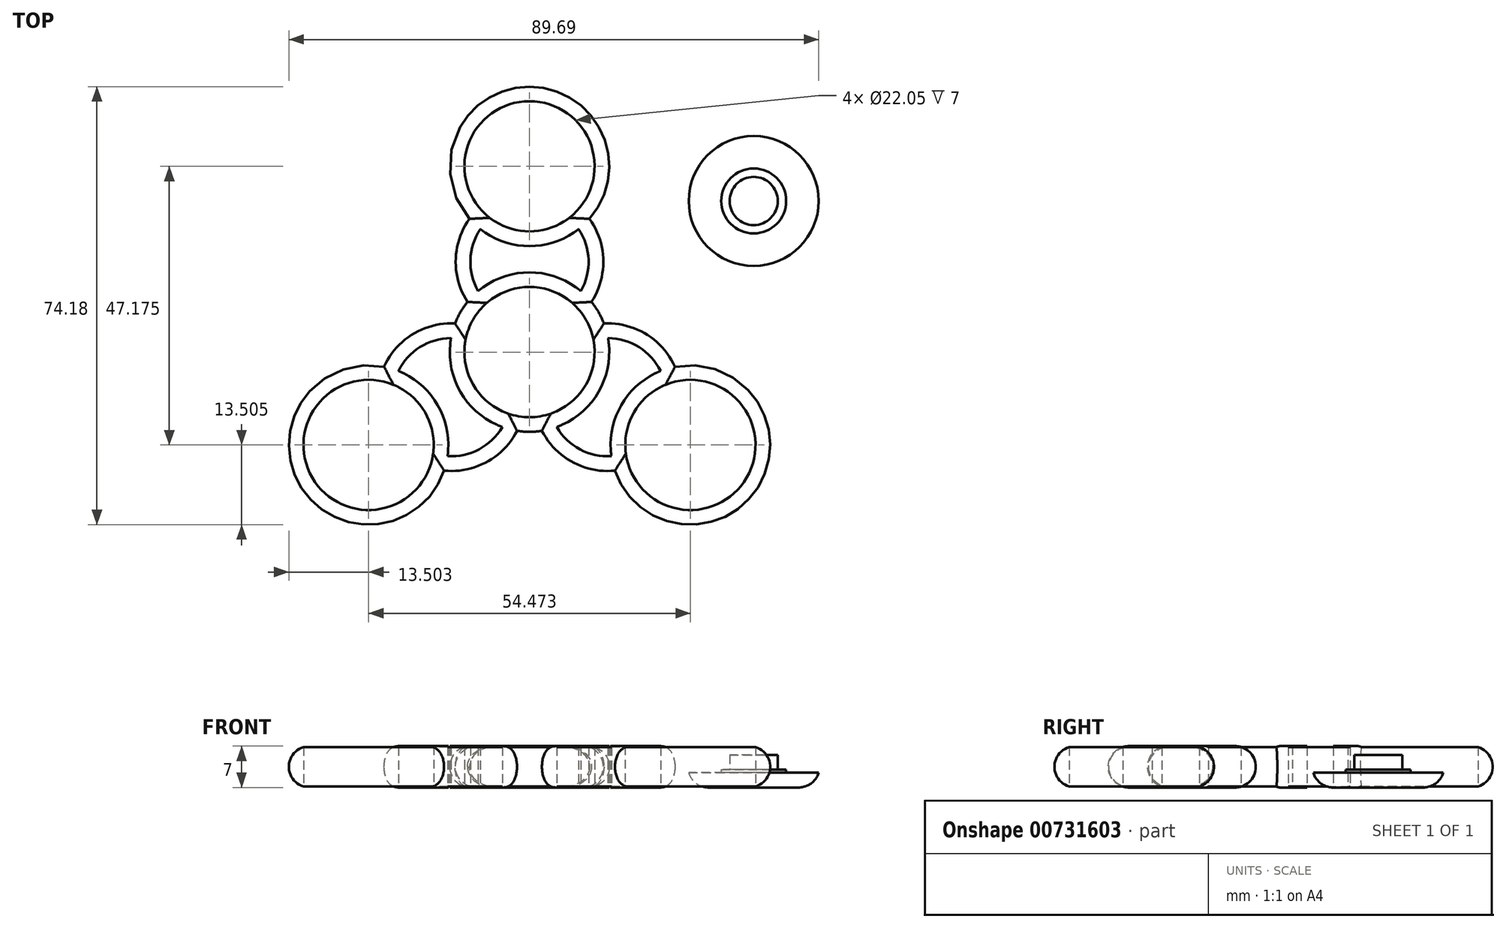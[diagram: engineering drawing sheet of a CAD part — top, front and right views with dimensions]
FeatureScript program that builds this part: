
annotation { "Feature Type Name" : "Feature", "Feature Type Description" : "" }
export const myFeature = defineFeature(function(context is Context, id is Id, definition is map)
    precondition{}
    {
        {
            var Q0;
            Q0=qCreatedBy(makeId("Top.planeOp"),FACE);
            var sketch = newSketch(context, id + "F0", { "sketchPlane" : qUnion([Q0])});
            skCircle(sketch, "E0", {"center": v(37.95, 25.58) * mm, "radius": 11 * mm});
            skCircle(sketch, "E1", {"center": v(37.95, 25.58) * mm, "radius": 4.08 * mm});
            skCircle(sketch, "E2", {"center": v(37.95, 25.58) * mm, "radius": 5.5 * mm});
            skSolve(sketch);
        }
        {
            var Q0;
            Q0=makeQuery(id+"F0.imprint","IMPRINT",FACE,{"disambiguationData":[TD([[makeQuery(id+"F0.imprint","IMPRINT",EDGE,{"derivedFrom":sQuery(id+"F0.wireOp",EDGE,"E0")}),1.0]])]});
            extrude(context, id + "F1", {"entities" : qUnion([Q0]), "depth" : 2.5 * mm, "offsetDistance" : 25 * mm});
        }
        {
            var Q0;
            Q0=makeQuery(id+"F0.imprint","IMPRINT",FACE,{"disambiguationData":[TD([[makeQuery(id+"F0.imprint","IMPRINT",EDGE,{"derivedFrom":sQuery(id+"F0.wireOp",EDGE,"E1")}),-1.0]])]});
            extrude(context, id + "F2", {"entities" : qUnion([Q0]), "operationType" : NewBodyOperationType.ADD, "depth" : 3 * mm, "offsetDistance" : 25 * mm});
        }
        {
            var Q0;
            Q0=makeQuery(id+"F0.imprint","IMPRINT",FACE,{"disambiguationData":[TD([[makeQuery(id+"F0.imprint","IMPRINT",EDGE,{"derivedFrom":sQuery(id+"F0.wireOp",EDGE,"E1")}),1.0]])]});
            extrude(context, id + "F3", {"entities" : qUnion([Q0]), "operationType" : NewBodyOperationType.ADD, "depth" : 5.5 * mm, "offsetDistance" : 25 * mm});
        }
        {
            var Q0;
            Q0=qCreatedBy(makeId("Top.planeOp"),FACE);
            var sketch = newSketch(context, id + "F4", { "sketchPlane" : qUnion([Q0])});
            skCircle(sketch, "E3", {"center": v(0, 0) * mm, "radius": 11.03 * mm});
            skCircle(sketch, "E4", {"center": v(0, 31.45) * mm, "radius": 11.03 * mm});
            skCircle(sketch, "E5", {"center": v(0, 0) * mm, "radius": 13.5 * mm});
            skCircle(sketch, "E6", {"center": v(0, 31.45) * mm, "radius": 13.5 * mm});
            skCircle(sketch, "E7", {"center": v(0, 15.28) * mm, "radius": 10 * mm});
            skCircle(sketch, "E8", {"center": v(0, 15.28) * mm, "radius": 12.5 * mm});
            skSolve(sketch);
        }
        {
            var Q0;
            Q0 = qSketchRegion(id + "F4", true);
            var Q1;
            {var subQ0=sQuery(id+"F4.wireOp",EDGE,"E7");var subQ1=sQuery(id+"F4.wireOp",EDGE,"E3");var subQ2=makeQuery(id+"F4.imprint","INTERSECT",VERTEX,{"disambiguationData":[OD(0.0)],"derivedFrom":[subQ1,subQ0]});Q1=makeQuery(id+"F4.imprint","IMPRINT",FACE,{"disambiguationData":[TD([[makeQuery(id+"F4.imprint","IMPRINT",EDGE,{"disambiguationData":[TD([[subQ2,-1.0]])],"derivedFrom":subQ1}),-1.0]])]});}
            var Q2;
            {var subQ0=sQuery(id+"F4.wireOp",EDGE,"E7");var subQ1=sQuery(id+"F4.wireOp",EDGE,"E4");var subQ2=makeQuery(id+"F4.imprint","INTERSECT",VERTEX,{"disambiguationData":[OD(0.0)],"derivedFrom":[subQ1,subQ0]});Q2=makeQuery(id+"F4.imprint","IMPRINT",FACE,{"disambiguationData":[TD([[makeQuery(id+"F4.imprint","IMPRINT",EDGE,{"disambiguationData":[TD([[subQ2,-1.0]])],"derivedFrom":subQ1}),-1.0]])]});}
            extrude(context, id + "F5", {"entities" : qUnion([Q0, Q1, Q2]), "depth" : 7 * mm, "offsetDistance" : 25 * mm});
        }
        {
            var Q0;
            Q0=makeQuery(id+"F5.opExtrude","SWEPT_BODY",BODY,{"disambiguationData":[OSD([sQuery(id+"F4.wireOp",EDGE,"E3"),sQuery(id+"F4.wireOp",EDGE,"E4"),sQuery(id+"F4.wireOp",EDGE,"E5"),sQuery(id+"F4.wireOp",EDGE,"E6"),sQuery(id+"F4.wireOp",EDGE,"E7"),sQuery(id+"F4.wireOp",EDGE,"E8")])]});
            var Q1;
            Q1=makeQuery(id+"F5.opExtrude","CAP_EDGE",EDGE,{"disambiguationData":[OSD([sQuery(id+"F4.wireOp",EDGE,"E3")])],"isStart":false});
            circularPattern(context, id + "F6", {"entities" : qUnion([Q0]), "axis" : qUnion([Q1]), "angle" : 360 * degree, "instanceCount" : 3, "equalSpace" : true});
        }
        {
            var Q0;
            Q0=makeQuery(id+"F6.opPattern","COPY",BODY,{"derivedFrom":makeQuery(id+"F5.opExtrude","SWEPT_BODY",BODY,{"disambiguationData":[OSD([sQuery(id+"F4.wireOp",EDGE,"E3"),sQuery(id+"F4.wireOp",EDGE,"E4"),sQuery(id+"F4.wireOp",EDGE,"E5"),sQuery(id+"F4.wireOp",EDGE,"E6"),sQuery(id+"F4.wireOp",EDGE,"E7"),sQuery(id+"F4.wireOp",EDGE,"E8")])]}),"instanceName":"1"});
            var Q1;
            Q1=makeQuery(id+"F6.opPattern","COPY",BODY,{"derivedFrom":makeQuery(id+"F5.opExtrude","SWEPT_BODY",BODY,{"disambiguationData":[OSD([sQuery(id+"F4.wireOp",EDGE,"E3"),sQuery(id+"F4.wireOp",EDGE,"E4"),sQuery(id+"F4.wireOp",EDGE,"E5"),sQuery(id+"F4.wireOp",EDGE,"E6"),sQuery(id+"F4.wireOp",EDGE,"E7"),sQuery(id+"F4.wireOp",EDGE,"E8")])]}),"instanceName":"2"});
            var Q2;
            Q2=makeQuery(id+"F5.opExtrude","SWEPT_BODY",BODY,{"disambiguationData":[OSD([sQuery(id+"F4.wireOp",EDGE,"E3"),sQuery(id+"F4.wireOp",EDGE,"E4"),sQuery(id+"F4.wireOp",EDGE,"E5"),sQuery(id+"F4.wireOp",EDGE,"E6"),sQuery(id+"F4.wireOp",EDGE,"E7"),sQuery(id+"F4.wireOp",EDGE,"E8")])]});
            booleanBodies(context, id + "F7", {"operationType" : BooleanOperationType.UNION, "tools" : qUnion([Q0, Q1, Q2])});
        }
        {
            var Q0;
            {var subQ0=sQuery(id+"F4.wireOp",EDGE,"E8");var subQ1=sQuery(id+"F4.wireOp",EDGE,"E6");Q0=makeQuery(id+"F6.opPattern","COPY",EDGE,{"derivedFrom":makeQuery(id+"F5.opExtrude","CAP_EDGE",EDGE,{"disambiguationData":[OSD([subQ1]),TDD([makeQuery(id+"F4.imprint","IMPRINT",EDGE,{"disambiguationData":[TD([[makeQuery(id+"F4.imprint","INTERSECT",VERTEX,{"disambiguationData":[OD(0.0)],"derivedFrom":[subQ1,subQ0]}),1.0]])],"derivedFrom":subQ1})])],"isStart":false}),"instanceName":"1"});}
            var Q1;
            {var subQ0=sQuery(id+"F4.wireOp",EDGE,"E8");var subQ1=sQuery(id+"F4.wireOp",EDGE,"E6");Q1=makeQuery(id+"F6.opPattern","COPY",EDGE,{"derivedFrom":makeQuery(id+"F5.opExtrude","CAP_EDGE",EDGE,{"disambiguationData":[OSD([subQ1]),TDD([makeQuery(id+"F4.imprint","IMPRINT",EDGE,{"disambiguationData":[TD([[makeQuery(id+"F4.imprint","INTERSECT",VERTEX,{"disambiguationData":[OD(0.0)],"derivedFrom":[subQ1,subQ0]}),1.0]])],"derivedFrom":subQ1})])],"isStart":true}),"instanceName":"1"});}
            var Q2;
            {var subQ0=sQuery(id+"F4.wireOp",EDGE,"E8");Q2=makeQuery(id+"F6.opPattern","COPY",EDGE,{"derivedFrom":makeQuery(id+"F5.opExtrude","CAP_EDGE",EDGE,{"disambiguationData":[OSD([subQ0]),TDD([makeQuery(id+"F4.imprint","IMPRINT",EDGE,{"disambiguationData":[TD([[makeQuery(id+"F4.imprint","INTERSECT",VERTEX,{"disambiguationData":[OD(1.0)],"derivedFrom":[sQuery(id+"F4.wireOp",EDGE,"E5"),subQ0]}),1.0]])],"derivedFrom":subQ0})])],"isStart":true}),"instanceName":"1"});}
            var Q3;
            {var subQ0=sQuery(id+"F4.wireOp",EDGE,"E8");var subQ1=sQuery(id+"F4.wireOp",EDGE,"E5");var subQ2=makeQuery(id+"F4.imprint","INTERSECT",VERTEX,{"disambiguationData":[OD(1.0)],"derivedFrom":[subQ1,subQ0]});var subQ4=makeQuery(id+"F4.imprint","INTERSECT",VERTEX,{"disambiguationData":[OD(0.0)],"derivedFrom":[subQ1,subQ0]});var subQ5=makeQuery(id+"F4.imprint","IMPRINT",EDGE,{"disambiguationData":[TD([[subQ4,1.0]])],"derivedFrom":subQ1});Q3=makeQuery(id+"F7.opBoolean","SPLIT",EDGE,{"disambiguationData":[TD([makeQuery(id+"F6.opPattern","COPY",FACE,{"derivedFrom":makeQuery(id+"F5.opExtrude","SWEPT_FACE",FACE,{"disambiguationData":[OSD([subQ0]),TDD([makeQuery(id+"F4.imprint","IMPRINT",EDGE,{"disambiguationData":[TD([[subQ2,1.0]])],"derivedFrom":subQ0})])]}),"instanceName":"1"})])],"derivedFrom":makeQuery(id+"F6.opPattern","COPY",EDGE,{"derivedFrom":makeQuery(id+"F5.opExtrude","CAP_EDGE",EDGE,{"disambiguationData":[OSD([subQ1]),TDD([subQ5])],"isStart":false}),"instanceName":"1"})});}
            var Q4;
            {var subQ0=sQuery(id+"F4.wireOp",EDGE,"E8");var subQ2=sQuery(id+"F4.wireOp",EDGE,"E5");var subQ4=makeQuery(id+"F4.imprint","INTERSECT",VERTEX,{"disambiguationData":[OD(0.0)],"derivedFrom":[subQ2,subQ0]});var subQ5=makeQuery(id+"F4.imprint","INTERSECT",VERTEX,{"disambiguationData":[OD(1.0)],"derivedFrom":[subQ2,subQ0]});var subQ6=makeQuery(id+"F4.imprint","IMPRINT",EDGE,{"disambiguationData":[TD([[subQ4,1.0]])],"derivedFrom":subQ2});Q4=makeQuery(id+"F7.opBoolean","SPLIT",EDGE,{"disambiguationData":[TD([makeQuery(id+"F6.opPattern","COPY",FACE,{"derivedFrom":makeQuery(id+"F5.opExtrude","SWEPT_FACE",FACE,{"disambiguationData":[OSD([subQ0]),TDD([makeQuery(id+"F4.imprint","IMPRINT",EDGE,{"disambiguationData":[TD([[subQ5,1.0]])],"derivedFrom":subQ0})])]}),"instanceName":"1"})])],"derivedFrom":makeQuery(id+"F6.opPattern","COPY",EDGE,{"derivedFrom":makeQuery(id+"F5.opExtrude","CAP_EDGE",EDGE,{"disambiguationData":[OSD([subQ2]),TDD([subQ6])],"isStart":true}),"instanceName":"1"})});}
            var Q5;
            {var subQ0=sQuery(id+"F4.wireOp",EDGE,"E8");Q5=makeQuery(id+"F6.opPattern","COPY",EDGE,{"derivedFrom":makeQuery(id+"F5.opExtrude","CAP_EDGE",EDGE,{"disambiguationData":[OSD([subQ0]),TDD([makeQuery(id+"F4.imprint","IMPRINT",EDGE,{"disambiguationData":[TD([[makeQuery(id+"F4.imprint","INTERSECT",VERTEX,{"disambiguationData":[OD(0.0)],"derivedFrom":[sQuery(id+"F4.wireOp",EDGE,"E5"),subQ0]}),-1.0]])],"derivedFrom":subQ0})])],"isStart":false}),"instanceName":"2"});}
            var Q6;
            {var subQ0=sQuery(id+"F4.wireOp",EDGE,"E8");Q6=makeQuery(id+"F6.opPattern","COPY",EDGE,{"derivedFrom":makeQuery(id+"F5.opExtrude","CAP_EDGE",EDGE,{"disambiguationData":[OSD([subQ0]),TDD([makeQuery(id+"F4.imprint","IMPRINT",EDGE,{"disambiguationData":[TD([[makeQuery(id+"F4.imprint","INTERSECT",VERTEX,{"disambiguationData":[OD(0.0)],"derivedFrom":[sQuery(id+"F4.wireOp",EDGE,"E5"),subQ0]}),-1.0]])],"derivedFrom":subQ0})])],"isStart":true}),"instanceName":"2"});}
            var Q7;
            {var subQ0=sQuery(id+"F4.wireOp",EDGE,"E8");var subQ1=sQuery(id+"F4.wireOp",EDGE,"E6");Q7=makeQuery(id+"F6.opPattern","COPY",EDGE,{"derivedFrom":makeQuery(id+"F5.opExtrude","CAP_EDGE",EDGE,{"disambiguationData":[OSD([subQ1]),TDD([makeQuery(id+"F4.imprint","IMPRINT",EDGE,{"disambiguationData":[TD([[makeQuery(id+"F4.imprint","INTERSECT",VERTEX,{"disambiguationData":[OD(0.0)],"derivedFrom":[subQ1,subQ0]}),1.0]])],"derivedFrom":subQ1})])],"isStart":false}),"instanceName":"2"});}
            var Q8;
            {var subQ0=sQuery(id+"F4.wireOp",EDGE,"E8");var subQ1=sQuery(id+"F4.wireOp",EDGE,"E6");Q8=makeQuery(id+"F6.opPattern","COPY",EDGE,{"derivedFrom":makeQuery(id+"F5.opExtrude","CAP_EDGE",EDGE,{"disambiguationData":[OSD([subQ1]),TDD([makeQuery(id+"F4.imprint","IMPRINT",EDGE,{"disambiguationData":[TD([[makeQuery(id+"F4.imprint","INTERSECT",VERTEX,{"disambiguationData":[OD(0.0)],"derivedFrom":[subQ1,subQ0]}),1.0]])],"derivedFrom":subQ1})])],"isStart":true}),"instanceName":"2"});}
            var Q9;
            {var subQ0=sQuery(id+"F4.wireOp",EDGE,"E8");Q9=makeQuery(id+"F6.opPattern","COPY",EDGE,{"derivedFrom":makeQuery(id+"F5.opExtrude","CAP_EDGE",EDGE,{"disambiguationData":[OSD([subQ0]),TDD([makeQuery(id+"F4.imprint","IMPRINT",EDGE,{"disambiguationData":[TD([[makeQuery(id+"F4.imprint","INTERSECT",VERTEX,{"disambiguationData":[OD(1.0)],"derivedFrom":[sQuery(id+"F4.wireOp",EDGE,"E5"),subQ0]}),1.0]])],"derivedFrom":subQ0})])],"isStart":false}),"instanceName":"1"});}
            var Q10;
            {var subQ0=sQuery(id+"F4.wireOp",EDGE,"E8");Q10=makeQuery(id+"F6.opPattern","COPY",EDGE,{"derivedFrom":makeQuery(id+"F5.opExtrude","CAP_EDGE",EDGE,{"disambiguationData":[OSD([subQ0]),TDD([makeQuery(id+"F4.imprint","IMPRINT",EDGE,{"disambiguationData":[TD([[makeQuery(id+"F4.imprint","INTERSECT",VERTEX,{"disambiguationData":[OD(1.0)],"derivedFrom":[sQuery(id+"F4.wireOp",EDGE,"E5"),subQ0]}),1.0]])],"derivedFrom":subQ0})])],"isStart":false}),"instanceName":"2"});}
            var Q11;
            {var subQ0=sQuery(id+"F4.wireOp",EDGE,"E8");Q11=makeQuery(id+"F6.opPattern","COPY",EDGE,{"derivedFrom":makeQuery(id+"F5.opExtrude","CAP_EDGE",EDGE,{"disambiguationData":[OSD([subQ0]),TDD([makeQuery(id+"F4.imprint","IMPRINT",EDGE,{"disambiguationData":[TD([[makeQuery(id+"F4.imprint","INTERSECT",VERTEX,{"disambiguationData":[OD(1.0)],"derivedFrom":[sQuery(id+"F4.wireOp",EDGE,"E5"),subQ0]}),1.0]])],"derivedFrom":subQ0})])],"isStart":true}),"instanceName":"2"});}
            var Q12;
            {var subQ0=sQuery(id+"F4.wireOp",EDGE,"E8");var subQ2=sQuery(id+"F4.wireOp",EDGE,"E5");var subQ4=makeQuery(id+"F4.imprint","INTERSECT",VERTEX,{"disambiguationData":[OD(0.0)],"derivedFrom":[subQ2,subQ0]});var subQ6=makeQuery(id+"F4.imprint","IMPRINT",EDGE,{"disambiguationData":[TD([[subQ4,1.0]])],"derivedFrom":subQ2});Q12=makeQuery(id+"F7.opBoolean","SPLIT",EDGE,{"disambiguationData":[TD([makeQuery(id+"F5.opExtrude","SWEPT_FACE",FACE,{"disambiguationData":[OSD([subQ0]),TDD([makeQuery(id+"F4.imprint","IMPRINT",EDGE,{"disambiguationData":[TD([[subQ4,-1.0]])],"derivedFrom":subQ0})])]})])],"derivedFrom":makeQuery(id+"F6.opPattern","COPY",EDGE,{"derivedFrom":makeQuery(id+"F5.opExtrude","CAP_EDGE",EDGE,{"disambiguationData":[OSD([subQ2]),TDD([subQ6])],"isStart":false}),"instanceName":"1"})});}
            var Q13;
            {var subQ0=sQuery(id+"F4.wireOp",EDGE,"E8");var subQ2=sQuery(id+"F4.wireOp",EDGE,"E5");var subQ4=makeQuery(id+"F4.imprint","INTERSECT",VERTEX,{"disambiguationData":[OD(0.0)],"derivedFrom":[subQ2,subQ0]});var subQ6=makeQuery(id+"F4.imprint","IMPRINT",EDGE,{"disambiguationData":[TD([[subQ4,1.0]])],"derivedFrom":subQ2});Q13=makeQuery(id+"F7.opBoolean","SPLIT",EDGE,{"disambiguationData":[TD([makeQuery(id+"F5.opExtrude","SWEPT_FACE",FACE,{"disambiguationData":[OSD([subQ0]),TDD([makeQuery(id+"F4.imprint","IMPRINT",EDGE,{"disambiguationData":[TD([[subQ4,-1.0]])],"derivedFrom":subQ0})])]})])],"derivedFrom":makeQuery(id+"F6.opPattern","COPY",EDGE,{"derivedFrom":makeQuery(id+"F5.opExtrude","CAP_EDGE",EDGE,{"disambiguationData":[OSD([subQ2]),TDD([subQ6])],"isStart":true}),"instanceName":"1"})});}
            var Q14;
            {var subQ0=sQuery(id+"F4.wireOp",EDGE,"E8");Q14=makeQuery(id+"F5.opExtrude","CAP_EDGE",EDGE,{"disambiguationData":[OSD([subQ0]),TDD([makeQuery(id+"F4.imprint","IMPRINT",EDGE,{"disambiguationData":[TD([[makeQuery(id+"F4.imprint","INTERSECT",VERTEX,{"disambiguationData":[OD(0.0)],"derivedFrom":[sQuery(id+"F4.wireOp",EDGE,"E5"),subQ0]}),-1.0]])],"derivedFrom":subQ0})])],"isStart":false});}
            var Q15;
            {var subQ0=sQuery(id+"F4.wireOp",EDGE,"E8");Q15=makeQuery(id+"F5.opExtrude","CAP_EDGE",EDGE,{"disambiguationData":[OSD([subQ0]),TDD([makeQuery(id+"F4.imprint","IMPRINT",EDGE,{"disambiguationData":[TD([[makeQuery(id+"F4.imprint","INTERSECT",VERTEX,{"disambiguationData":[OD(0.0)],"derivedFrom":[sQuery(id+"F4.wireOp",EDGE,"E5"),subQ0]}),-1.0]])],"derivedFrom":subQ0})])],"isStart":true});}
            var Q16;
            {var subQ0=sQuery(id+"F4.wireOp",EDGE,"E8");var subQ1=sQuery(id+"F4.wireOp",EDGE,"E6");Q16=makeQuery(id+"F5.opExtrude","CAP_EDGE",EDGE,{"disambiguationData":[OSD([subQ1]),TDD([makeQuery(id+"F4.imprint","IMPRINT",EDGE,{"disambiguationData":[TD([[makeQuery(id+"F4.imprint","INTERSECT",VERTEX,{"disambiguationData":[OD(0.0)],"derivedFrom":[subQ1,subQ0]}),1.0]])],"derivedFrom":subQ1})])],"isStart":false});}
            var Q17;
            {var subQ0=sQuery(id+"F4.wireOp",EDGE,"E8");Q17=makeQuery(id+"F5.opExtrude","CAP_EDGE",EDGE,{"disambiguationData":[OSD([subQ0]),TDD([makeQuery(id+"F4.imprint","IMPRINT",EDGE,{"disambiguationData":[TD([[makeQuery(id+"F4.imprint","INTERSECT",VERTEX,{"disambiguationData":[OD(1.0)],"derivedFrom":[sQuery(id+"F4.wireOp",EDGE,"E5"),subQ0]}),1.0]])],"derivedFrom":subQ0})])],"isStart":true});}
            var Q18;
            {var subQ0=sQuery(id+"F4.wireOp",EDGE,"E8");Q18=makeQuery(id+"F6.opPattern","COPY",EDGE,{"derivedFrom":makeQuery(id+"F5.opExtrude","CAP_EDGE",EDGE,{"disambiguationData":[OSD([subQ0]),TDD([makeQuery(id+"F4.imprint","IMPRINT",EDGE,{"disambiguationData":[TD([[makeQuery(id+"F4.imprint","INTERSECT",VERTEX,{"disambiguationData":[OD(0.0)],"derivedFrom":[sQuery(id+"F4.wireOp",EDGE,"E5"),subQ0]}),-1.0]])],"derivedFrom":subQ0})])],"isStart":true}),"instanceName":"1"});}
            var Q19;
            {var subQ0=sQuery(id+"F4.wireOp",EDGE,"E8");var subQ1=sQuery(id+"F4.wireOp",EDGE,"E5");var subQ2=makeQuery(id+"F4.imprint","INTERSECT",VERTEX,{"disambiguationData":[OD(0.0)],"derivedFrom":[subQ1,subQ0]});var subQ3=makeQuery(id+"F4.imprint","INTERSECT",VERTEX,{"disambiguationData":[OD(1.0)],"derivedFrom":[subQ1,subQ0]});var subQ4=makeQuery(id+"F4.imprint","IMPRINT",EDGE,{"disambiguationData":[TD([[subQ2,1.0]])],"derivedFrom":subQ1});Q19=makeQuery(id+"F7.opBoolean","SPLIT",EDGE,{"disambiguationData":[TD([makeQuery(id+"F5.opExtrude","SWEPT_FACE",FACE,{"disambiguationData":[OSD([subQ0]),TDD([makeQuery(id+"F4.imprint","IMPRINT",EDGE,{"disambiguationData":[TD([[subQ3,1.0]])],"derivedFrom":subQ0})])]})])],"derivedFrom":makeQuery(id+"F6.opPattern","COPY",EDGE,{"derivedFrom":makeQuery(id+"F5.opExtrude","CAP_EDGE",EDGE,{"disambiguationData":[OSD([subQ1]),TDD([subQ4])],"isStart":false}),"instanceName":"1"})});}
            var Q20;
            {var subQ0=sQuery(id+"F4.wireOp",EDGE,"E8");var subQ2=sQuery(id+"F4.wireOp",EDGE,"E5");var subQ4=makeQuery(id+"F4.imprint","INTERSECT",VERTEX,{"disambiguationData":[OD(1.0)],"derivedFrom":[subQ2,subQ0]});var subQ5=makeQuery(id+"F4.imprint","INTERSECT",VERTEX,{"disambiguationData":[OD(0.0)],"derivedFrom":[subQ2,subQ0]});var subQ6=makeQuery(id+"F4.imprint","IMPRINT",EDGE,{"disambiguationData":[TD([[subQ5,1.0]])],"derivedFrom":subQ2});Q20=makeQuery(id+"F7.opBoolean","SPLIT",EDGE,{"disambiguationData":[TD([makeQuery(id+"F5.opExtrude","SWEPT_FACE",FACE,{"disambiguationData":[OSD([subQ0]),TDD([makeQuery(id+"F4.imprint","IMPRINT",EDGE,{"disambiguationData":[TD([[subQ4,1.0]])],"derivedFrom":subQ0})])]})])],"derivedFrom":makeQuery(id+"F6.opPattern","COPY",EDGE,{"derivedFrom":makeQuery(id+"F5.opExtrude","CAP_EDGE",EDGE,{"disambiguationData":[OSD([subQ2]),TDD([subQ6])],"isStart":true}),"instanceName":"1"})});}
            var Q21;
            {var subQ0=sQuery(id+"F4.wireOp",EDGE,"E8");Q21=makeQuery(id+"F6.opPattern","COPY",EDGE,{"derivedFrom":makeQuery(id+"F5.opExtrude","CAP_EDGE",EDGE,{"disambiguationData":[OSD([subQ0]),TDD([makeQuery(id+"F4.imprint","IMPRINT",EDGE,{"disambiguationData":[TD([[makeQuery(id+"F4.imprint","INTERSECT",VERTEX,{"disambiguationData":[OD(0.0)],"derivedFrom":[sQuery(id+"F4.wireOp",EDGE,"E5"),subQ0]}),-1.0]])],"derivedFrom":subQ0})])],"isStart":false}),"instanceName":"1"});}
            var Q22;
            {var subQ0=sQuery(id+"F4.wireOp",EDGE,"E8");Q22=makeQuery(id+"F5.opExtrude","CAP_EDGE",EDGE,{"disambiguationData":[OSD([subQ0]),TDD([makeQuery(id+"F4.imprint","IMPRINT",EDGE,{"disambiguationData":[TD([[makeQuery(id+"F4.imprint","INTERSECT",VERTEX,{"disambiguationData":[OD(1.0)],"derivedFrom":[sQuery(id+"F4.wireOp",EDGE,"E5"),subQ0]}),1.0]])],"derivedFrom":subQ0})])],"isStart":false});}
            var Q23;
            {var subQ0=sQuery(id+"F4.wireOp",EDGE,"E8");var subQ1=sQuery(id+"F4.wireOp",EDGE,"E6");Q23=makeQuery(id+"F5.opExtrude","CAP_EDGE",EDGE,{"disambiguationData":[OSD([subQ1]),TDD([makeQuery(id+"F4.imprint","IMPRINT",EDGE,{"disambiguationData":[TD([[makeQuery(id+"F4.imprint","INTERSECT",VERTEX,{"disambiguationData":[OD(0.0)],"derivedFrom":[subQ1,subQ0]}),1.0]])],"derivedFrom":subQ1})])],"isStart":true});}
            var Q24;
            Q24=makeQuery(id+"F1.opExtrude","CAP_EDGE",EDGE,{"disambiguationData":[OSD([sQuery(id+"F0.wireOp",EDGE,"E0")])],"isStart":true});
            fillet(context, id + "F8", {"entities" : qUnion([Q0, Q1, Q2, Q3, Q4, Q5, Q6, Q7, Q8, Q9, Q10, Q11, Q12, Q13, Q14, Q15, Q16, Q17, Q18, Q19, Q20, Q21, Q22, Q23, Q24]), "radius" : 3.5 * mm, "tangentPropagation" : true, "allowEdgeOverflow" : false});
        }
    });
